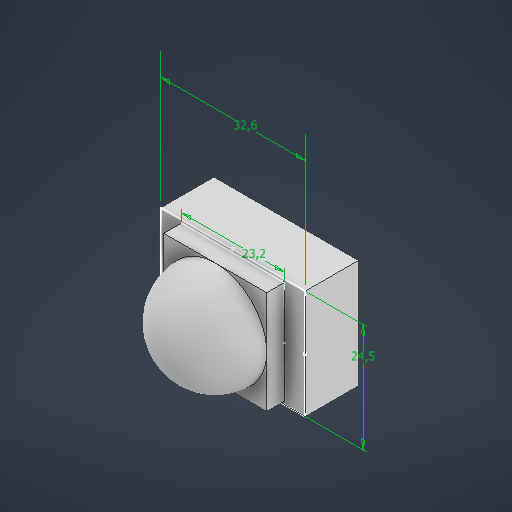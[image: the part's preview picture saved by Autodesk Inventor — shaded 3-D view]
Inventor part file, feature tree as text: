
AUTODESK INVENTOR PART (.ipt)
format: ipt  version: 2025.2 (Build 292293000, 293)  size: 227,328 bytes
history: native  units: mm
features: sketch x2, extrude x2, revolve x1
ambient origin geometry x8: Origin, YZ Plane, XZ Plane, XY Plane, X Axis, Y Axis, Z Axis, Center Point
bodies: Solid1 (feature_tree)
feature tree (5):
  sketch  "Sketch1"  dims[d0=32.6mm d1=24.5mm]
  extrude  "Extrusion1"  Depth=24.5mm
  extrude  "Extrusion2"  Depth=12.0mm TaperAngle=0.0deg
  revolve  "Revolution1"  [1 undecoded]
  sketch  "Sketch2"  dims[d2=23.2mm d3=12.0mm d4=0.0mm d5=4.0mm d6=0.0mm d7=90.0deg]
note: 1 required parameter value undecoded (feature->parameter linkage not recoverable at this tier; creation-order binding heuristic only, values carry confidence <= 0.55)
